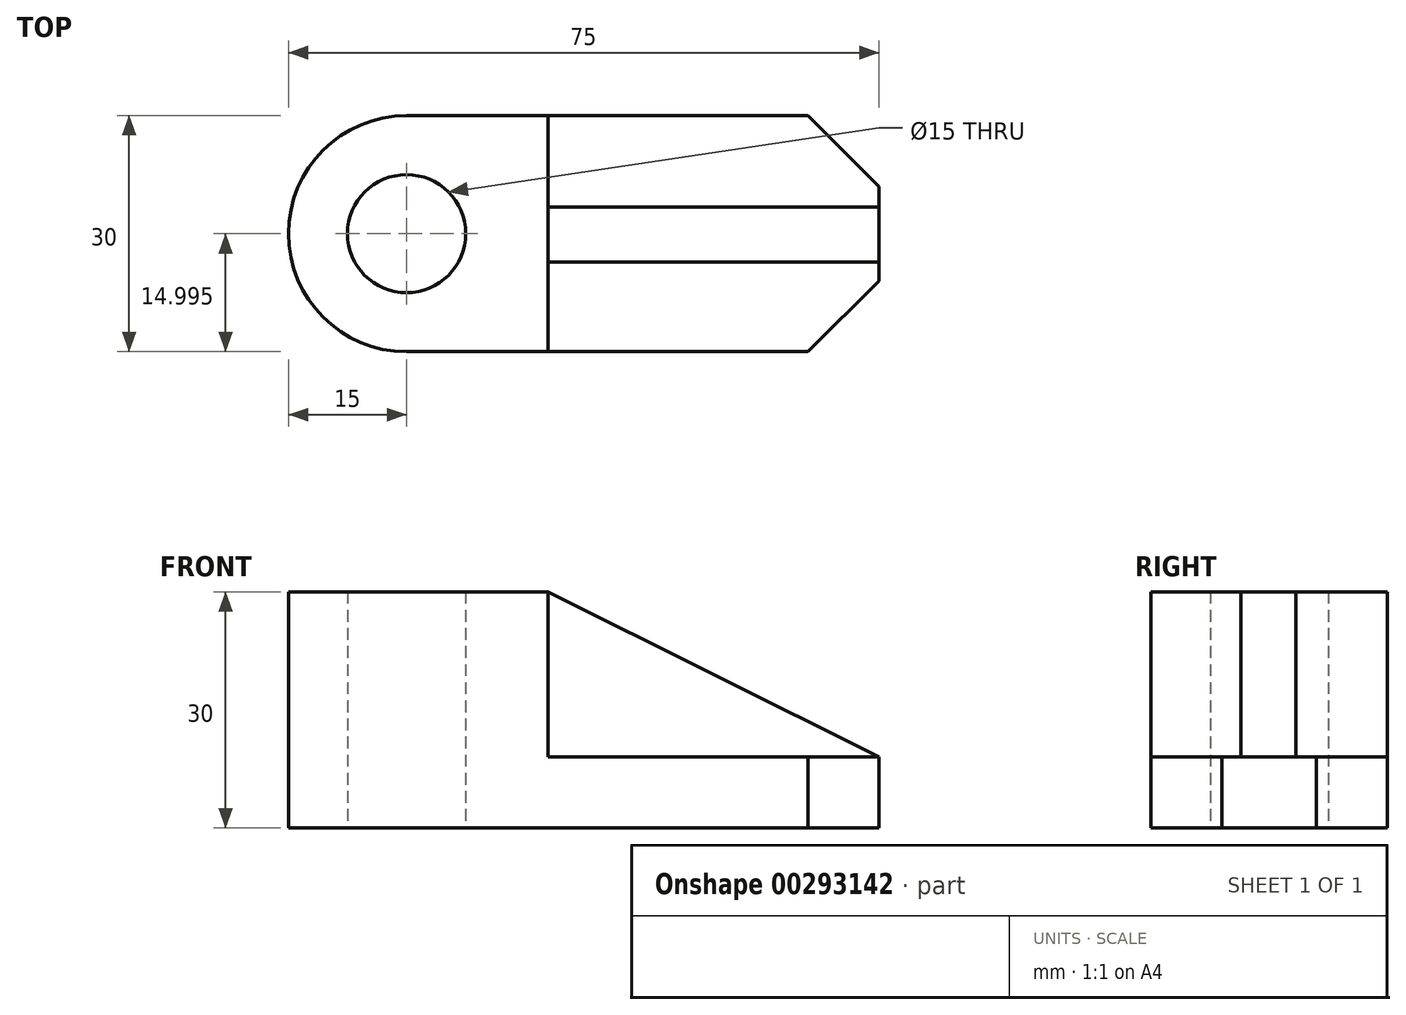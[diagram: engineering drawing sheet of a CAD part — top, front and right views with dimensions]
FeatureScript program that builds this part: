
annotation { "Feature Type Name" : "Feature", "Feature Type Description" : "" }
export const myFeature = defineFeature(function(context is Context, id is Id, definition is map)
    precondition{}
    {
        {
            var Q0;
            Q0=qCreatedBy(makeId("Top.planeOp"),FACE);
            var sketch = newSketch(context, id + "F0", { "sketchPlane" : qUnion([Q0])});
            skArc(sketch, "E0", {"start": v(-13.29, 13.83) * mm, "mid": v(-28.29, -1.17) * mm, "end": v(-13.29, -16.17) * mm});
            skLineSegment(sketch, "E1", {"start": v(-13.29, 13.83) * mm, "end": v(4.71, 13.83) * mm});
            skLineSegment(sketch, "E2", {"start": v(4.71, 13.83) * mm, "end": v(4.71, 2.33) * mm});
            skLineSegment(sketch, "E3", {"start": v(4.71, -16.17) * mm, "end": v(-13.29, -16.17) * mm});
            skCircle(sketch, "E4", {"center": v(-13.29, -1.17) * mm, "radius": 7.5 * mm});
            skLineSegment(sketch, "E5", {"start": v(4.71, 13.83) * mm, "end": v(37.71, 13.83) * mm});
            skLineSegment(sketch, "E6", {"start": v(37.71, 13.83) * mm, "end": v(46.71, 4.83) * mm});
            skLineSegment(sketch, "E7", {"start": v(46.71, 4.83) * mm, "end": v(46.71, -7.17) * mm});
            skLineSegment(sketch, "E8", {"start": v(46.71, -7.17) * mm, "end": v(37.71, -16.17) * mm});
            skLineSegment(sketch, "E9", {"start": v(37.71, -16.17) * mm, "end": v(4.71, -16.17) * mm});
            skLineSegment(sketch, "E10", {"start": v(-28.29, -1.17) * mm, "end": v(46.71, -1.17) * mm, "construction": true});
            skLineSegment(sketch, "E11", {"start": v(4.71, 2.33) * mm, "end": v(46.71, 2.33) * mm});
            skLineSegment(sketch, "E12", {"start": v(4.71, -4.67) * mm, "end": v(46.71, -4.67) * mm});
            skLineSegment(sketch, "E13.trimOffspring", {"start": v(4.71, -4.67) * mm, "end": v(4.71, -16.17) * mm});
            skLineSegment(sketch, "E14", {"start": v(4.71, 2.33) * mm, "end": v(4.71, -4.67) * mm});
            skSolve(sketch);
        }
        {
            var Q0;
            Q0=makeQuery(id+"F0.imprint","IMPRINT",FACE,{"disambiguationData":[TD([[makeQuery(id+"F0.imprint","IMPRINT",EDGE,{"derivedFrom":sQuery(id+"F0.wireOp",EDGE,"E2")}),1.0]])]});
            var Q1;
            {var subQ1=sQuery(id+"F0.wireOp",EDGE,"E8");Q1=makeQuery(id+"F0.imprint","IMPRINT",FACE,{"disambiguationData":[TD([[makeQuery(id+"F0.imprint","IMPRINT",EDGE,{"derivedFrom":subQ1}),-1.0]])]});}
            var Q2;
            {var subQ0=sQuery(id+"F0.wireOp",EDGE,"E11");Q2=makeQuery(id+"F0.imprint","IMPRINT",FACE,{"disambiguationData":[TD([[makeQuery(id+"F0.imprint","IMPRINT",EDGE,{"derivedFrom":subQ0}),-1.0]])]});}
            extrude(context, id + "F1", {"entities" : qUnion([Q0, Q1, Q2]), "depth" : 9 * mm});
        }
        {
            var Q0;
            Q0=makeQuery(id+"F0.imprint","IMPRINT",FACE,{"disambiguationData":[TD([[makeQuery(id+"F0.imprint","IMPRINT",EDGE,{"derivedFrom":sQuery(id+"F0.wireOp",EDGE,"E0")}),1.0]])]});
            extrude(context, id + "F2", {"entities" : qUnion([Q0]), "operationType" : NewBodyOperationType.ADD, "depth" : 30 * mm});
        }
        {
            var Q0;
            Q0=makeQuery(id+"F2.boolean.opBoolean","MERGE",FACE,{"derivedFrom":[makeQuery(id+"F1.opExtrude","SWEPT_FACE",FACE,{"disambiguationData":[OSD([sQuery(id+"F0.wireOp",EDGE,"E9")])]}),makeQuery(id+"F2.opExtrude","SWEPT_FACE",FACE,{"disambiguationData":[OSD([sQuery(id+"F0.wireOp",EDGE,"E3")])]})]});
            var sketch = newSketch(context, id + "F3", { "sketchPlane" : qUnion([Q0])});
            skLineSegment(sketch, "E15.0", {"start": v(4.71, 30) * mm, "end": v(4.71, 9) * mm});
            skLineSegment(sketch, "E15.1", {"start": v(37.71, 9) * mm, "end": v(4.71, 9) * mm});
            skLineSegment(sketch, "E15.2", {"start": v(46.71, 9) * mm, "end": v(37.71, 9) * mm});
            skLineSegment(sketch, "E16", {"start": v(4.71, 30) * mm, "end": v(46.71, 9) * mm});
            skLineSegment(sketch, "E17", {"start": v(4.71, 9) * mm, "end": v(4.71, 30) * mm});
            skSolve(sketch);
        }
        {
            var Q0;
            Q0=makeQuery(id+"F3.imprint","IMPRINT",FACE,{"disambiguationData":[TD([[makeQuery(id+"F3.imprint","IMPRINT",EDGE,{"derivedFrom":sQuery(id+"F3.wireOp",EDGE,"E15.1")}),-1.0]])]});
            extrude(context, id + "F4", {"entities" : qUnion([Q0]), "operationType" : NewBodyOperationType.ADD, "endBound" : BoundingType.SYMMETRIC, "oppositeDirection" : true, "depth" : 36.8 * mm});
        }
        {
            var Q0;
            Q0=makeQuery(id+"F4.opExtrude","CAP_FACE",FACE,{"disambiguationData":[OSD([sQuery(id+"F3.wireOp",EDGE,"E15.1"),sQuery(id+"F3.wireOp",EDGE,"E15.2"),sQuery(id+"F3.wireOp",EDGE,"E16"),sQuery(id+"F3.wireOp",EDGE,"E17")])],"isStart":true});
            extrude(context, id + "F5", {"entities" : qUnion([Q0]), "operationType" : NewBodyOperationType.REMOVE, "oppositeDirection" : true, "depth" : 29.8 * mm});
        }
    });
